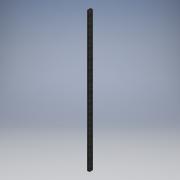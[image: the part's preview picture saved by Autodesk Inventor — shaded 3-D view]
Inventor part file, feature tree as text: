
AUTODESK INVENTOR PART (.ipt)
format: ipt  version: 2018 (Build 220112000, 112)  size: 129,536 bytes
history: native  units: mm
features: extrude x2, sketch x2, other x1
ambient origin geometry x8: Origin, YZ Plane, XZ Plane, XY Plane, X Axis, Y Axis, Z Axis, Center Point
bodies: Body1 (feature_tree)
feature tree (5):
  other  "Sólido1"
  extrude  "Extrusión1"  Depth=40.0mm
  extrude  "Extrusión3"  Depth=2570.0mm TaperAngle=0.0deg
  sketch  "Boceto1"  dims[d0=60.0mm d1=40.0mm]
  sketch  "Boceto2"  dims[d2=2.0mm d3=2570.0mm d4=0.0mm d5=10.0mm d6=214.0mm d9=10.0mm d10=214.0mm d11=10.0mm d12=214.0mm d13=10.0mm d14=214.0mm d15=10.0mm d16=214.0mm d17=215.0mm d18=2.0mm d19=0.0mm]
